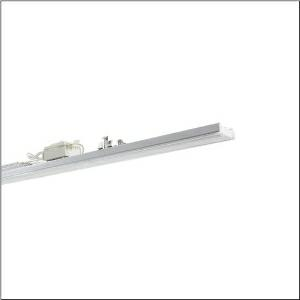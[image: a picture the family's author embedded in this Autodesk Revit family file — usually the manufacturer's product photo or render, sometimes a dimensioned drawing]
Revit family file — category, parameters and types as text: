
# Revit family: licross_21_recessed_ho_52tl11dn4dxs
name_source: partatom
category: Lighting Fixtures
units: mm (PartAtom-declared; Revit-internal decimal feet)

## family parameters
Cut with Voids When Loaded = No
Host = Face
Light Source = No
Part Type = Normal
Room Calculation Point = No
Round Connector Dimension = Use Diameter
Shared = No

## types (1)
- --- (1 x LED, 13000 lm, 72.5 W, 4000K)
    Apparent Load = 73 VA
    CIE Flux Codes = 87 95 99 100 100
    Color Rendering = 80
    Color Temperature = 4000K
    Default Elevation = 1800 mm
    Description = Licross 21 Recessed HO, luminaire insert, of sheet steel, galvanised, coil coated, white, length: 1.500mm, width: 66mm, height: 67mm, LED rated luminous flux: 13.000lm, light colour: 840, SDCM (Standard Deviation of Colour Matching)MacAdam ≤ 3 SDCM (initial), control gear: DALI 2, with plug, 5-pole, with phase selection, mains connection: 220..240V, AC, 50/60Hz, rated input power: 73W, internal wiring halogen-free, primary light control with lens, of plastic, primary optical cover: cover, of PMMA, light emission: direct distribution, primary light characteristic: symmetric, protection rating (complete): IP40, insulation class (complete): insulation class I (protective earthing), certification: CE, ENEC, VDE, UKCA, protection symbol: D if used in an environment without relevant dust loads with corresponding accessories, impact resistance: IK06, permissible ambient temperature for indoor applications: -25..+35°C, corresponds to IFS (International Featured Standards) requirements for safety and quality in the food industry, reducing of maximum allowable ambient temperature of 5°C with ceiling mounting, LABS conformity tested according to VDMA 24364:2018-05, The light source and the operating device comply with the requirements of the Ecodesign Regulation (EU) 2019/2020 and are replaceable in accordance with this regulation, packaging unit: 1 piece
    Height = 58 mm
    Lamp = 1 x LED
    Lamp Light Flux = 13000 lm
    Lamp Power = 72.5 W
    Lamp count = 1
    Length = 1500 mm
    Luminous efficacy = 179 lm/W
    Manufacturer = Siteco
    ModVariant = No
    Model = 52TL11DN4DXS
    Mounting Place = Ceiling
    Mounting Type = Pendant
    Number of Poles = 1
    OnlyDefault = Yes
    Power Factor = 1
    Product Name = Licross 21 Recessed HO
    Product group = luminaire insert | ceiling pendant
    ProductGroupID = 901
    Protection Class = Protection class I
    Protection Degree = IP 40
    RLX_Detail_Level = 1
    RLX_Emergency_Light_Flux = 0 lm
    RLX_Emergency_Type = 0
    RLX_Emergency_Type_DB = No
    RlxData = <blob elided: 24813 chars, md5=3ed8bf6a>
    Socket = socket
    Standby Power = 0 W
    System Light Flux = 13000 lm
    System Power = 73 W
    Type Comments = factory setting: luminous flux: 100 % | dim-lin: 254 | 415 mA
    Type Image = l_1296930.jpg
    URL = http://relux.com
    VarID = @adj_127379
    Voltage = 0 V
    Weight = 0.00 kg
    Width = 66 mm

## geometry (parser evidence)
native form markers: Blend x4, Sweep x10
no freeform markers — native parametric forms only
